# Revit family: Haworth_Epure_ProximityStorage_UpperModule_EU_PRELIMINARY
name_source: partatom
category: Furniture
units: mm (PartAtom-declared; Revit-internal decimal feet)

## family parameters
Always vertical = Yes
Cut with Voids When Loaded = No
OmniClass Number = 23.40.70.14.64.11
OmniClass Title = Office Furniture
Room Calculation Point = No
Shared = No
Work Plane-Based = No

## types (2) — shared parameters
Actual Depth = 45 cm
Actual Height = 46 cm
Actual Width = 80 cm
Assembly Code = E2020200
Description = Haworth - Epure - Proximity Storage - Upper Module
Handle 1 = No
Handle 2 = No
Manufacturer = Haworth
Model = EUPSINTXTXM
Mounting Height = 25 cm
Revision Number = 1
Size = Verify Final Dim.w/ Haworth
Thickness for bottom = 1.9, 2.5, 3.6 cm
Trim Finish = Haworth _ Paint _ Smooth Plaster
URL = https://www.haworth.com
URL - Product = https://www.haworth.com
Warranty = http://www.haworth.com
without Pull = No

## per-type parameters (varying)
| type | Metal Handle | Thickness Bottom | with Pull | with Shelf |
| Stackable Open | No | 2 cm | No | Yes |
| Stackable with Tambour Door | Yes | 4 cm | Yes | No |

type visibility flags: 2 boolean params named "<type name>" — each type sets only its own to Yes (folded from table)

## geometry (parser evidence)
native form markers: Sweep x5
no freeform markers — native parametric forms only
